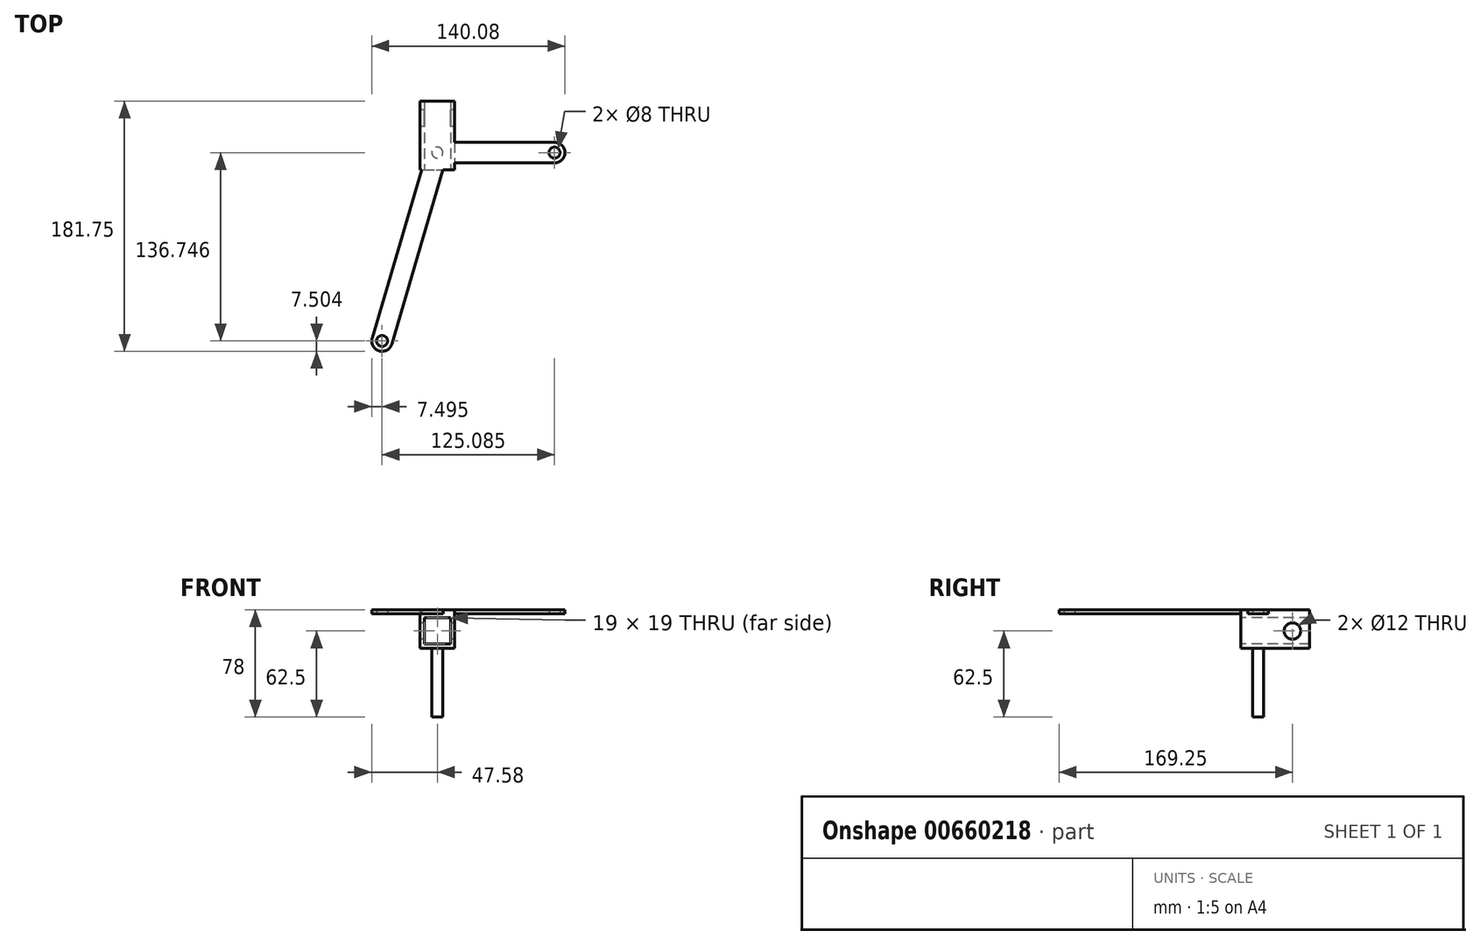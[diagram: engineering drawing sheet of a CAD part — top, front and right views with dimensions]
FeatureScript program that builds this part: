
annotation { "Feature Type Name" : "Feature", "Feature Type Description" : "" }
export const myFeature = defineFeature(function(context is Context, id is Id, definition is map)
    precondition{}
    {
        {
            var Q0;
            Q0=qCreatedBy(makeId("Top.planeOp"),FACE);
            var sketch = newSketch(context, id + "F0", { "sketchPlane" : qUnion([Q0])});
            skLineSegment(sketch, "E0.bottom", {"start": v(12.5, 7.5) * mm, "end": v(85, 7.5) * mm});
            skLineSegment(sketch, "E0.top", {"start": v(12.5, -7.5) * mm, "end": v(85, -7.5) * mm});
            skLineSegment(sketch, "E0.right", {"start": v(92.5, 0) * mm, "end": v(92.5, 0) * mm});
            skCircle(sketch, "E1", {"center": v(85, 0) * mm, "radius": 4 * mm});
            skLineSegment(sketch, "E2", {"start": v(0, 0) * mm, "end": v(-42.2, -143.94) * mm, "construction": true});
            skLineSegment(sketch, "E3", {"start": v(-42.2, -143.94) * mm, "end": v(-42.2, -143.94) * mm});
            skLineSegment(sketch, "E4", {"start": v(-47.28, -134.64) * mm, "end": v(-11.48, -12.5) * mm});
            skLineSegment(sketch, "E5", {"start": v(-32.89, -138.86) * mm, "end": v(4.04, -12.9) * mm});
            skPoint(sketch, "E6.orphan", {"position": v(-56.59, -139.72) * mm});
            skPoint(sketch, "E7.orphan", {"position": v(0, 26.66) * mm});
            skCircle(sketch, "E8", {"center": v(-40.08, -136.75) * mm, "radius": 4 * mm});
            skPoint(sketch, "E9.visualSharp", {"position": v(-49.4, -141.83) * mm});
            skArc(sketch, "E9.filletArc", {"start": v(-47.28, -134.64) * mm, "mid": v(-46.67, -140.34) * mm, "end": v(-42.2, -143.94) * mm});
            skPoint(sketch, "E10.visualSharp", {"position": v(-35, -146.05) * mm});
            skArc(sketch, "E10.filletArc", {"start": v(-42.2, -143.94) * mm, "mid": v(-36.49, -143.33) * mm, "end": v(-32.89, -138.86) * mm});
            skPoint(sketch, "E11.visualSharp", {"position": v(92.5, 7.5) * mm});
            skArc(sketch, "E11.filletArc", {"start": v(92.5, 0) * mm, "mid": v(90.3, 5.3) * mm, "end": v(85, 7.5) * mm});
            skPoint(sketch, "E12.visualSharp", {"position": v(92.5, -7.5) * mm});
            skArc(sketch, "E12.filletArc", {"start": v(85, -7.5) * mm, "mid": v(90.3, -5.3) * mm, "end": v(92.5, 0) * mm});
            skPoint(sketch, "E13.visualSharp", {"position": v(5.62, -7.5) * mm});
            skArc(sketch, "E13.filletArc", {"start": v(4.16, -12.5) * mm, "mid": v(4.1, -12.7) * mm, "end": v(4.04, -12.9) * mm});
            skLineSegment(sketch, "E14.bottom", {"start": v(-12.5, 37.5) * mm, "end": v(12.5, 37.5) * mm});
            skLineSegment(sketch, "E14.top", {"start": v(-12.5, -12.5) * mm, "end": v(-11.48, -12.5) * mm});
            skLineSegment(sketch, "E14.left", {"start": v(-12.5, 37.5) * mm, "end": v(-12.5, -12.5) * mm});
            skLineSegment(sketch, "E14.right", {"start": v(12.5, 37.5) * mm, "end": v(12.5, 7.5) * mm});
            skPoint(sketch, "E0.left.start.orphan", {"position": v(-7.5, 7.5) * mm});
            skLineSegment(sketch, "E15.trimOffspring", {"start": v(4.16, -12.5) * mm, "end": v(12.5, -12.5) * mm});
            skLineSegment(sketch, "E16.trimOffspring", {"start": v(12.5, -7.5) * mm, "end": v(12.5, -12.5) * mm});
            skLineSegment(sketch, "E17", {"start": v(357.5, 1219.58) * mm, "end": v(0, 0) * mm, "construction": true});
            skSolve(sketch);
        }
        {
            var Q0;
            Q0=makeQuery(id+"F0.imprint","IMPRINT",FACE,{"disambiguationData":[TD([[makeQuery(id+"F0.imprint","IMPRINT",EDGE,{"derivedFrom":sQuery(id+"F0.wireOp",EDGE,"E0.bottom")}),-1.0]])]});
            extrude(context, id + "F1", {"entities" : qUnion([Q0]), "depth" : 3 * mm, "offsetDistance" : 25 * mm});
        }
        {
            var Q0;
            Q0=makeQuery(id+"F1.opExtrude","CAP_FACE",FACE,{"disambiguationData":[OSD([sQuery(id+"F0.wireOp",EDGE,"E0.bottom"),sQuery(id+"F0.wireOp",EDGE,"E0.top"),sQuery(id+"F0.wireOp",EDGE,"E0.left"),sQuery(id+"F0.wireOp",EDGE,"E1"),sQuery(id+"F0.wireOp",EDGE,"E4"),sQuery(id+"F0.wireOp",EDGE,"E5"),sQuery(id+"F0.wireOp",EDGE,"E8"),sQuery(id+"F0.wireOp",EDGE,"E9.filletArc"),sQuery(id+"F0.wireOp",EDGE,"E10.filletArc"),sQuery(id+"F0.wireOp",EDGE,"E11.filletArc"),sQuery(id+"F0.wireOp",EDGE,"E12.filletArc"),sQuery(id+"F0.wireOp",EDGE,"E13.filletArc")])],"isStart":false});
            var sketch = newSketch(context, id + "F2", { "sketchPlane" : qUnion([Q0])});
            skLineSegment(sketch, "E18.bottom", {"start": v(-12.5, 37.5) * mm, "end": v(12.5, 37.5) * mm});
            skLineSegment(sketch, "E18.top", {"start": v(-12.5, -12.5) * mm, "end": v(12.5, -12.5) * mm});
            skLineSegment(sketch, "E18.left", {"start": v(-12.5, 37.5) * mm, "end": v(-12.5, -12.5) * mm});
            skLineSegment(sketch, "E18.right", {"start": v(12.5, 37.5) * mm, "end": v(12.5, -12.5) * mm});
            skSolve(sketch);
        }
        {
            var Q0;
            Q0=qSketchRegion(id+"F2",true);
            extrude(context, id + "F3", {"entities" : qUnion([Q0]), "operationType" : NewBodyOperationType.ADD, "oppositeDirection" : true, "depth" : 28 * mm, "offsetDistance" : 25 * mm});
        }
        {
            var Q0;
            Q0=makeQuery(id+"F3.opExtrude","CAP_FACE",FACE,{"disambiguationData":[OSD([sQuery(id+"F2.wireOp",EDGE,"E18.bottom"),sQuery(id+"F2.wireOp",EDGE,"E18.top"),sQuery(id+"F2.wireOp",EDGE,"E18.left"),sQuery(id+"F2.wireOp",EDGE,"E18.right")])],"isStart":false});
            var sketch = newSketch(context, id + "F4", { "sketchPlane" : qUnion([Q0])});
            skCircle(sketch, "E19", {"center": v(0, 0) * mm, "radius": 4 * mm});
            skSolve(sketch);
        }
        {
            var Q0;
            Q0=makeQuery(id+"F3.boolean.opBoolean","MERGE",FACE,{"derivedFrom":[makeQuery(id+"F1.opExtrude","SWEPT_FACE",FACE,{"disambiguationData":[OSD([sQuery(id+"F0.wireOp",EDGE,"E14.left")])]}),makeQuery(id+"F3.opExtrude","SWEPT_FACE",FACE,{"disambiguationData":[OSD([sQuery(id+"F2.wireOp",EDGE,"E18.left")])]})]});
            var sketch = newSketch(context, id + "F5", { "sketchPlane" : qUnion([Q0])});
            skCircle(sketch, "E20", {"center": v(-25, -12.5) * mm, "radius": 6 * mm});
            skSolve(sketch);
        }
        {
            var Q0;
            Q0=qSketchRegion(id+"F5",true);
            extrude(context, id + "F6", {"entities" : qUnion([Q0]), "operationType" : NewBodyOperationType.REMOVE, "oppositeDirection" : true, "depth" : 25 * mm, "offsetDistance" : 25 * mm});
        }
        {
            var Q0;
            Q0=makeQuery(id+"F3.boolean.opBoolean","MERGE",FACE,{"derivedFrom":[makeQuery(id+"F1.opExtrude","SWEPT_FACE",FACE,{"disambiguationData":[OSD([sQuery(id+"F0.wireOp",EDGE,"E14.top")])]}),makeQuery(id+"F1.opExtrude","SWEPT_FACE",FACE,{"disambiguationData":[OSD([sQuery(id+"F0.wireOp",EDGE,"E15.trimOffspring")])]}),makeQuery(id+"F3.opExtrude","SWEPT_FACE",FACE,{"disambiguationData":[OSD([sQuery(id+"F2.wireOp",EDGE,"E18.top")])]})]});
            var sketch = newSketch(context, id + "F7", { "sketchPlane" : qUnion([Q0])});
            skLineSegment(sketch, "E21.bottom", {"start": v(-9.5, -3) * mm, "end": v(9.5, -3) * mm});
            skLineSegment(sketch, "E21.top", {"start": v(-9.5, -22) * mm, "end": v(9.5, -22) * mm});
            skLineSegment(sketch, "E21.left", {"start": v(-9.5, -3) * mm, "end": v(-9.5, -22) * mm});
            skLineSegment(sketch, "E21.right", {"start": v(9.5, -3) * mm, "end": v(9.5, -22) * mm});
            skSolve(sketch);
        }
        {
            var Q0;
            Q0 = qSketchRegion(id + "F7", true);
            extrude(context, id + "F8", {"entities" : qUnion([Q0]), "operationType" : NewBodyOperationType.REMOVE, "oppositeDirection" : true, "depth" : 50 * mm, "offsetDistance" : 25 * mm});
        }
        {
            var Q0;
            Q0=qSketchRegion(id+"F4",true);
            extrude(context, id + "F9", {"entities" : qUnion([Q0]), "operationType" : NewBodyOperationType.ADD, "depth" : 50 * mm, "offsetDistance" : 25 * mm});
        }
    });
